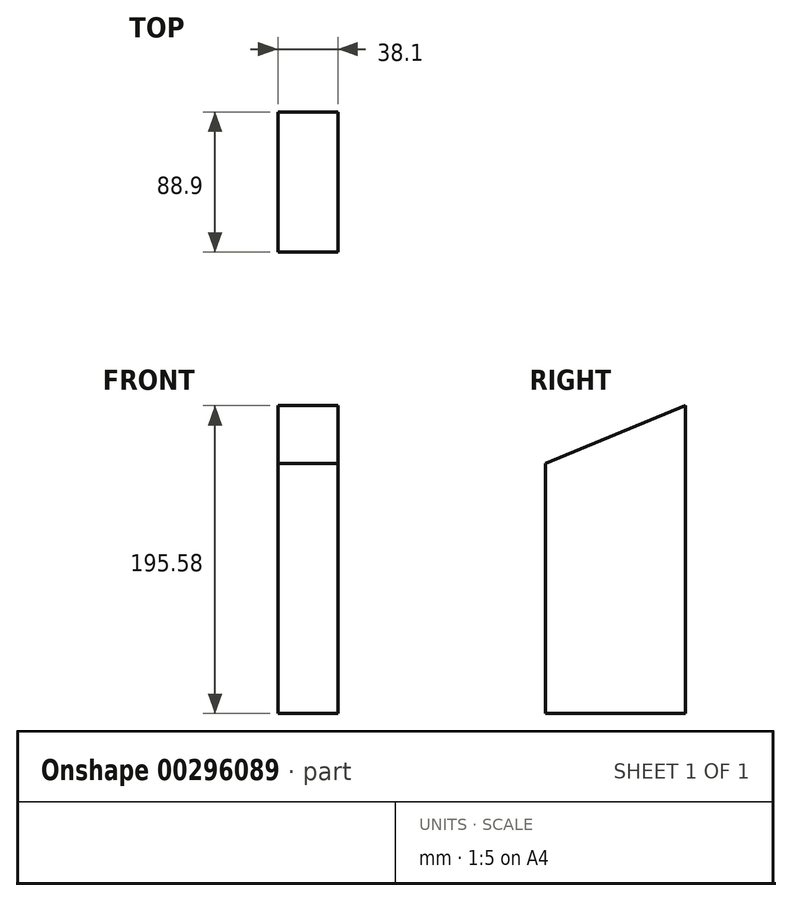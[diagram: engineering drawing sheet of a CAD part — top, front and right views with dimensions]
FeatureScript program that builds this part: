
annotation { "Feature Type Name" : "Feature", "Feature Type Description" : "" }
export const myFeature = defineFeature(function(context is Context, id is Id, definition is map)
    precondition{}
    {
        {
            var Q0;
            Q0=qCreatedBy(makeId("Right.planeOp"),FACE);
            var sketch = newSketch(context, id + "F0", { "sketchPlane" : qUnion([Q0])});
            skLineSegment(sketch, "E0", {"start": v(40.74, 119.44) * mm, "end": v(40.74, -76.14) * mm});
            skLineSegment(sketch, "E1", {"start": v(40.74, -76.14) * mm, "end": v(-48.16, -76.14) * mm});
            skLineSegment(sketch, "E2", {"start": v(-48.16, -76.14) * mm, "end": v(-48.16, 82.61) * mm});
            skLineSegment(sketch, "E3", {"start": v(-48.16, 82.61) * mm, "end": v(40.74, 119.44) * mm});
            skSolve(sketch);
        }
        {
            var Q0;
            Q0=makeQuery(id+"F0.imprint","IMPRINT",FACE,{"disambiguationData":[TD([[makeQuery(id+"F0.imprint","IMPRINT",EDGE,{"derivedFrom":sQuery(id+"F0.wireOp",EDGE,"E0")}),-1.0]])]});
            extrude(context, id + "F1", {"entities" : qUnion([Q0]), "depth" : 38.1 * mm});
        }
    });
